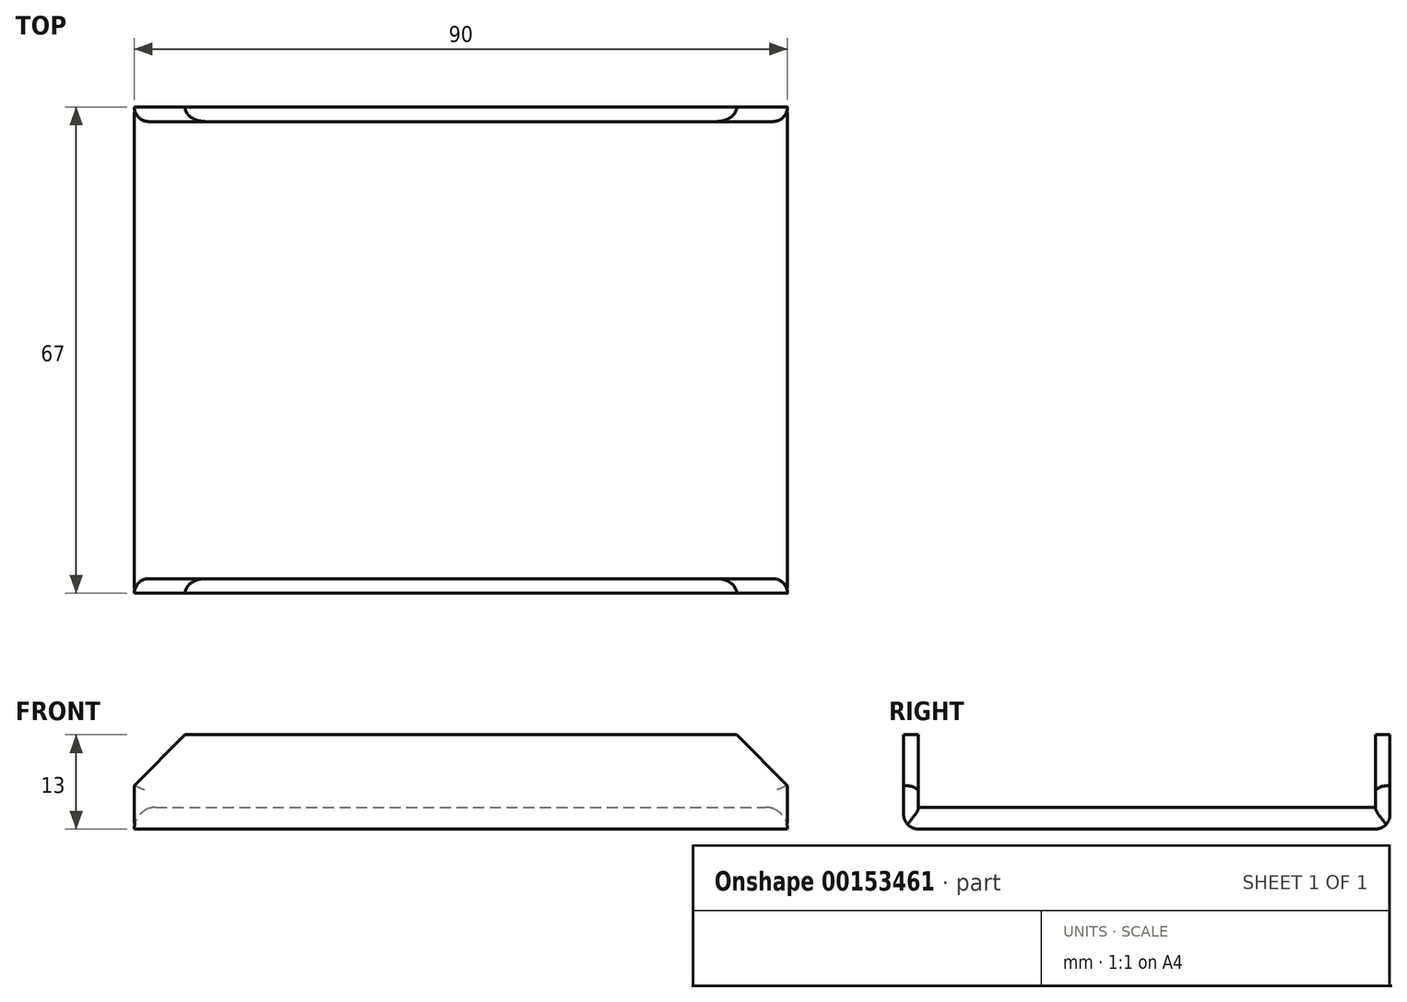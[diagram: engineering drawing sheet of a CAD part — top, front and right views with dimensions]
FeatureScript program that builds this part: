
annotation { "Feature Type Name" : "Feature", "Feature Type Description" : "" }
export const myFeature = defineFeature(function(context is Context, id is Id, definition is map)
    precondition{}
    {
        {
            var Q0;
            Q0=qCreatedBy(makeId("Top.planeOp"),FACE);
            var sketch = newSketch(context, id + "F0", { "sketchPlane" : qUnion([Q0])});
            skLineSegment(sketch, "E0.bottom", {"start": v(-46.2, 18.73) * mm, "end": v(43.8, 18.73) * mm});
            skLineSegment(sketch, "E0.top", {"start": v(-46.2, -48.27) * mm, "end": v(43.8, -48.27) * mm});
            skLineSegment(sketch, "E0.left", {"start": v(-46.2, 18.73) * mm, "end": v(-46.2, -48.27) * mm});
            skLineSegment(sketch, "E0.right", {"start": v(43.8, 18.73) * mm, "end": v(43.8, -48.27) * mm});
            skSolve(sketch);
        }
        {
            var Q0;
            Q0 = qSketchRegion(id + "F0", true);
            extrude(context, id + "F1", {"entities" : qUnion([Q0]), "depth" : 3 * mm});
        }
        {
            var Q0;
            Q0=makeQuery(id+"F1.opExtrude","CAP_FACE",FACE,{"disambiguationData":[OSD([sQuery(id+"F0.wireOp",EDGE,"E0.bottom"),sQuery(id+"F0.wireOp",EDGE,"E0.top"),sQuery(id+"F0.wireOp",EDGE,"E0.left"),sQuery(id+"F0.wireOp",EDGE,"E0.right")])],"isStart":false});
            var sketch = newSketch(context, id + "F2", { "sketchPlane" : qUnion([Q0])});
            skLineSegment(sketch, "E1.bottom", {"start": v(-46.2, 18.73) * mm, "end": v(43.8, 18.73) * mm});
            skLineSegment(sketch, "E1.top", {"start": v(-46.2, 16.73) * mm, "end": v(43.8, 16.73) * mm});
            skLineSegment(sketch, "E1.left", {"start": v(-46.2, 18.73) * mm, "end": v(-46.2, 16.73) * mm});
            skLineSegment(sketch, "E1.right", {"start": v(43.8, 18.73) * mm, "end": v(43.8, 16.73) * mm});
            skLineSegment(sketch, "E2.bottom", {"start": v(-46.2, -48.27) * mm, "end": v(43.8, -48.27) * mm});
            skLineSegment(sketch, "E2.top", {"start": v(-46.2, -46.27) * mm, "end": v(43.8, -46.27) * mm});
            skLineSegment(sketch, "E2.left", {"start": v(-46.2, -48.27) * mm, "end": v(-46.2, -46.27) * mm});
            skLineSegment(sketch, "E2.right", {"start": v(43.8, -48.27) * mm, "end": v(43.8, -46.27) * mm});
            skSolve(sketch);
        }
        {
            var Q0;
            Q0 = qSketchRegion(id + "F2", true);
            extrude(context, id + "F3", {"entities" : qUnion([Q0]), "operationType" : NewBodyOperationType.ADD, "depth" : 10 * mm});
        }
        {
            var Q0;
            Q0=makeQuery(id+"F3.opExtrude","CAP_EDGE",EDGE,{"disambiguationData":[OSD([sQuery(id+"F2.wireOp",EDGE,"E2.right")])],"isStart":false});
            var Q1;
            Q1=makeQuery(id+"F3.opExtrude","CAP_EDGE",EDGE,{"disambiguationData":[OSD([sQuery(id+"F2.wireOp",EDGE,"E1.right")])],"isStart":false});
            var Q2;
            Q2=makeQuery(id+"F3.opExtrude","CAP_EDGE",EDGE,{"disambiguationData":[OSD([sQuery(id+"F2.wireOp",EDGE,"E2.left")])],"isStart":false});
            var Q3;
            Q3=makeQuery(id+"F3.opExtrude","CAP_EDGE",EDGE,{"disambiguationData":[OSD([sQuery(id+"F2.wireOp",EDGE,"E1.left")])],"isStart":false});
            chamfer(context, id + "F4", {"entities" : qUnion([Q0, Q1, Q2, Q3]), "width" : 7 * mm, "tangentPropagation" : true});
        }
        {
            var Q0;
            Q0=makeQuery(id+"F1.opExtrude","CAP_EDGE",EDGE,{"disambiguationData":[OSD([sQuery(id+"F0.wireOp",EDGE,"E0.left")])],"isStart":false});
            var Q1;
            Q1=makeQuery(id+"F1.opExtrude","CAP_EDGE",EDGE,{"disambiguationData":[OSD([sQuery(id+"F0.wireOp",EDGE,"E0.right")])],"isStart":false});
            fillet(context, id + "F5", {"entities" : qUnion([Q0, Q1]), "radius" : 3 * mm, "tangentPropagation" : true, "allowEdgeOverflow" : false});
        }
        {
            var Q0;
            Q0=makeQuery(id+"F1.opExtrude","CAP_EDGE",EDGE,{"disambiguationData":[OSD([sQuery(id+"F0.wireOp",EDGE,"E0.top")])],"isStart":true});
            var Q1;
            Q1=makeQuery(id+"F1.opExtrude","CAP_EDGE",EDGE,{"disambiguationData":[OSD([sQuery(id+"F0.wireOp",EDGE,"E0.bottom")])],"isStart":true});
            fillet(context, id + "F6", {"entities" : qUnion([Q0, Q1]), "radius" : 2 * mm, "tangentPropagation" : true, "allowEdgeOverflow" : false});
        }
        {
            var Q0;
            Q0=makeQuery(id+"F4.opChamfer","BLEND_EDGE",EDGE,{"blendedFrom":[makeQuery(id+"F3.opExtrude","CAP_EDGE",EDGE,{"disambiguationData":[OSD([sQuery(id+"F2.wireOp",EDGE,"E2.left")])],"isStart":false}),makeQuery(id+"F3.opExtrude","SWEPT_FACE",FACE,{"disambiguationData":[OSD([sQuery(id+"F2.wireOp",EDGE,"E2.top")])]})],"blendedInto":[makeQuery(id+"F3.opExtrude","SWEPT_FACE",FACE,{"disambiguationData":[OSD([sQuery(id+"F2.wireOp",EDGE,"E2.top")])]})]});
            var Q1;
            Q1=makeQuery(id+"F4.opChamfer","BLEND_EDGE",EDGE,{"blendedFrom":[makeQuery(id+"F3.opExtrude","CAP_EDGE",EDGE,{"disambiguationData":[OSD([sQuery(id+"F2.wireOp",EDGE,"E1.left")])],"isStart":false}),makeQuery(id+"F3.opExtrude","SWEPT_FACE",FACE,{"disambiguationData":[OSD([sQuery(id+"F2.wireOp",EDGE,"E1.top")])]})],"blendedInto":[makeQuery(id+"F3.opExtrude","SWEPT_FACE",FACE,{"disambiguationData":[OSD([sQuery(id+"F2.wireOp",EDGE,"E1.top")])]})]});
            var Q2;
            Q2=makeQuery(id+"F4.opChamfer","BLEND_EDGE",EDGE,{"blendedFrom":[makeQuery(id+"F3.opExtrude","CAP_EDGE",EDGE,{"disambiguationData":[OSD([sQuery(id+"F2.wireOp",EDGE,"E1.right")])],"isStart":false}),makeQuery(id+"F3.opExtrude","SWEPT_FACE",FACE,{"disambiguationData":[OSD([sQuery(id+"F2.wireOp",EDGE,"E1.top")])]})],"blendedInto":[makeQuery(id+"F3.opExtrude","SWEPT_FACE",FACE,{"disambiguationData":[OSD([sQuery(id+"F2.wireOp",EDGE,"E1.top")])]})]});
            var Q3;
            Q3=makeQuery(id+"F4.opChamfer","BLEND_EDGE",EDGE,{"blendedFrom":[makeQuery(id+"F3.opExtrude","CAP_EDGE",EDGE,{"disambiguationData":[OSD([sQuery(id+"F2.wireOp",EDGE,"E2.right")])],"isStart":false}),makeQuery(id+"F3.opExtrude","SWEPT_FACE",FACE,{"disambiguationData":[OSD([sQuery(id+"F2.wireOp",EDGE,"E2.top")])]})],"blendedInto":[makeQuery(id+"F3.opExtrude","SWEPT_FACE",FACE,{"disambiguationData":[OSD([sQuery(id+"F2.wireOp",EDGE,"E2.top")])]})]});
            var Q4;
            Q4=makeQuery(id+"F3.opExtrude","SWEPT_EDGE",EDGE,{"disambiguationData":[OSD([sQuery(id+"F0.wireOp",EDGE,"E0.right"),sQuery(id+"F2.wireOp",EDGE,"E1.top"),sQuery(id+"F2.wireOp",EDGE,"E1.right")])]});
            var Q5;
            Q5=makeQuery(id+"F3.opExtrude","SWEPT_EDGE",EDGE,{"disambiguationData":[OSD([sQuery(id+"F0.wireOp",EDGE,"E0.right"),sQuery(id+"F2.wireOp",EDGE,"E2.top"),sQuery(id+"F2.wireOp",EDGE,"E2.right")])]});
            var Q6;
            Q6=makeQuery(id+"F3.opExtrude","SWEPT_EDGE",EDGE,{"disambiguationData":[OSD([sQuery(id+"F0.wireOp",EDGE,"E0.left"),sQuery(id+"F2.wireOp",EDGE,"E2.top"),sQuery(id+"F2.wireOp",EDGE,"E2.left")])]});
            var Q7;
            Q7=makeQuery(id+"F3.opExtrude","SWEPT_EDGE",EDGE,{"disambiguationData":[OSD([sQuery(id+"F0.wireOp",EDGE,"E0.left"),sQuery(id+"F2.wireOp",EDGE,"E1.top"),sQuery(id+"F2.wireOp",EDGE,"E1.left")])]});
            fillet(context, id + "F7", {"entities" : qUnion([Q0, Q1, Q2, Q3, Q4, Q5, Q6, Q7]), "radius" : 2 * mm, "tangentPropagation" : true, "allowEdgeOverflow" : false});
        }
    });
